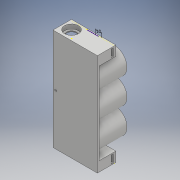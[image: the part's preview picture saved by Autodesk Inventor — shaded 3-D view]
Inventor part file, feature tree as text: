
AUTODESK INVENTOR PART (.ipt)
format: ipt  version: 2018 (Build 220112000, 112)  size: 730,112 bytes
history: native  units: mm
features: sketch x23, extrude x20, fillet x4
ambient origin geometry x8: Origin, YZ Plane, XZ Plane, XY Plane, X Axis, Y Axis, Z Axis, Center Point
bodies: Solid1 (feature_tree)
feature tree (47):
  extrude  "Extrusion1"  Depth=165.0mm
  extrude  "Extrusion2"  Depth=8.5mm
  extrude  "Extrusion3"  Depth=25.0mm TaperAngle=0.0deg
  extrude  "Extrusion4"  Depth=22.75mm
  extrude  "Extrusion5"  Depth=15.5mm
  extrude  "Extrusion6"  Depth=7.1mm TaperAngle=0.0deg
  fillet  "Fillet1"  Radius=5.0mm
  extrude  "Extrusion7"  Depth=10.0mm TaperAngle=0.0deg
  fillet  "Fillet2"  Radius=2.0mm
  extrude  "Extrusion8"  Depth=16.0mm
  extrude  "Extrusion9"  Depth=16.0mm
  fillet  "Fillet3"  Radius=8.0mm
  extrude  "Extrusion10"  Depth=6.0mm
  extrude  "Extrusion11"  Depth=12.25mm
  sketch  "Sketch12"  dims[d32=12.25mm d33=3.5mm]
  sketch  "Sketch13"  dims[d34=12.25mm d35=12.25mm]
  extrude  "Extrusion12"  Depth=12.25mm
  extrude  "Extrusion13"  Depth=12.25mm
  sketch  "Sketch16"  dims[d41=8.0mm d42=1.0mm]
  extrude  "Extrusion14"  Depth=40.0mm TaperAngle=0.0deg
  extrude  "Extrusion15"  Depth=2.0mm
  extrude  "Extrusion16"  Depth=1.0mm
  extrude  "Extrusion17"  Depth=2.0mm TaperAngle=0.0deg
  extrude  "Extrusion18"  Depth=7.1mm TaperAngle=0.0deg
  fillet  "Fillet4"  Radius=3.0mm
  extrude  "Extrusion19"  Depth=42.0mm
  extrude  "Extrusion20"  Depth=42.0mm
  sketch  "Sketch1"  dims[d0=25.0mm d1=165.0mm]
  sketch  "Sketch2"  dims[d2=3.0mm d3=0.0mm d4=8.5mm]
  sketch  "Sketch3"  dims[d5=8.5mm d6=25.0mm d7=0.0mm]
  sketch  "Sketch4"  dims[d8=25.0mm d9=22.75mm]
  sketch  "Sketch5"  dims[d10=7.1mm d11=0.0mm d12=15.5mm]
  sketch  "Sketch6"  dims[d13=165.0mm d14=0.0mm d15=7.1mm d16=0.0mm d17=5.0mm]
  sketch  "Sketch7"  dims[d18=5.0mm d19=10.0mm d20=0.0mm d21=2.0mm]
  sketch  "Sketch8"  dims[d22=16.0mm d23=8.0mm]
  sketch  "Sketch9"  dims[d24=16.0mm d25=16.0mm d26=8.0mm]
  sketch  "Sketch10"  dims[d27=45.0mm d28=0.0mm d29=6.0mm]
  sketch  "Sketch11"  dims[d30=12.25mm d31=3.5mm]
  sketch  "Sketch14"  dims[d36=3.5mm d37=40.0mm d38=0.0mm]
  sketch  "Sketch15"  dims[d39=1.0mm d40=2.0mm]
  sketch  "Sketch17"  dims[d43=2.0mm d44=12.0mm d45=0.0mm]
  sketch  "Sketch18"  dims[d46=6.0mm d47=7.1mm d48=0.0mm d49=3.0mm d50=0.0mm]
  sketch  "Sketch19"  dims[d51=42.0mm d52=38.75mm]
  sketch  "Sketch20"  dims[d53=42.0mm d54=38.75mm]
  sketch  "Sketch21"  dims[d55=42.0mm]
  sketch  "Sketch22"  dims[d56=38.75mm]
  sketch  "Sketch23"  dims[d57=45.0mm d58=0.0mm d59=2.0mm d60=4.0mm d61=2.0mm d62=4.0mm d63=45.0mm d64=0.0mm d65=10.0mm d66=12.0mm d67=0.0mm d68=2.0mm d69=0.0mm d70=2.0mm d71=0.0mm d72=2.0mm d73=2.0mm d74=5.0mm d75=0.0mm d76=2.0mm d77=2.0mm d78=7.0mm d79=0.0mm d80=1.0mm d81=0.25mm d82=0.25mm d83=44.75mm d84=0.0mm d85=44.0mm d86=0.0mm]
